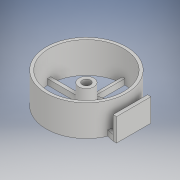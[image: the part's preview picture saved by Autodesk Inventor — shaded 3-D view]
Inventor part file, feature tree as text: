
AUTODESK INVENTOR PART (.ipt)
format: ipt  version: 2019 (Build 230136000, 136)  size: 252,928 bytes
history: native  units: in
note: dims shown in document units (in); Inventor stores cm internally (conversion verified against a paired STEP export)
features: sketch x13, extrude x12, projected_geometry x6
ambient origin geometry x8: Origin, YZ Plane, XZ Plane, XY Plane, X Axis, Y Axis, Z Axis, Center Point
bodies: Solid1 (feature_tree)
feature tree (31):
  extrude  "Extrusion1"  Depth=0.15in
  extrude  "Extrusion2"  Depth=0.1in TaperAngle=0.0deg
  extrude  "Extrusion3"  Depth=0.75in
  sketch  "Sketch6"  dims[d8=0.15in d9=0.25in d10=0.0in]
  extrude  "Extrusion7"  Depth=0.25in TaperAngle=0.0deg
  extrude  "Extrusion9"  Depth=0.875in TaperAngle=0.0deg
  extrude  "Extrusion10"  Depth=0.115in
  extrude  "Extrusion11"  Depth=0.05in
  extrude  "Extrusion12"  Depth=0.115in
  extrude  "Extrusion14"  Depth=0.05in
  extrude  "Extrusion15"  TaperAngle=0.0deg  [1 undecoded]
  extrude  "Extrusion16"  TaperAngle=0.0deg  [1 undecoded]
  extrude  "Extrusion17"  Depth=0.1in
  sketch  "Sketch1"  dims[d0=0.36in d1=0.15in]
  sketch  "Sketch2"  dims[d2=0.78in d3=0.0in d4=0.1in d5=0.0in]
  sketch  "Sketch3"  dims[d6=1.5in d7=0.75in]
  sketch  "Sketch10"  dims[d20=0.5315in d28=0.875in d29=0.0in]
  sketch  "Sketch13"  dims[d32=0.115in d33=0.115in]
  sketch  "Sketch14"  dims[d34=0.0675in d35=0.05in]
  projected_geometry  "Projected Loop9"
  projected_geometry  "Projected Loop10"
  projected_geometry  "Projected Loop11"
  projected_geometry  "Projected Loop12"
  sketch  "Sketch15"  dims[d36=0.115in d37=0.115in]
  sketch  "Sketch16"  dims[d38=0.068in d39=0.05in]
  sketch  "Sketch19"  dims[d40=0.15in d41=0.0in d42=0.0in]
  sketch  "Sketch20"  dims[d43=0.0in d44=0.0in]
  projected_geometry  "Projected Loop13"
  sketch  "Sketch21"  dims[d45=0.1in d46=0.0in d47=3.25in]
  projected_geometry  "Projected Loop14"
  sketch  "Sketch23"  dims[d48=3.5in d49=0.1in d50=0.0in d51=3.25in d52=1.25in d53=0.0in d82=0.25in d83=0.0in d84=0.25in d85=0.0in d86=0.25in d87=0.0in d88=0.75in d89=0.0in]
note: 2 required parameter values undecoded (feature->parameter linkage not recoverable at this tier; creation-order binding heuristic only, values carry confidence <= 0.55)
